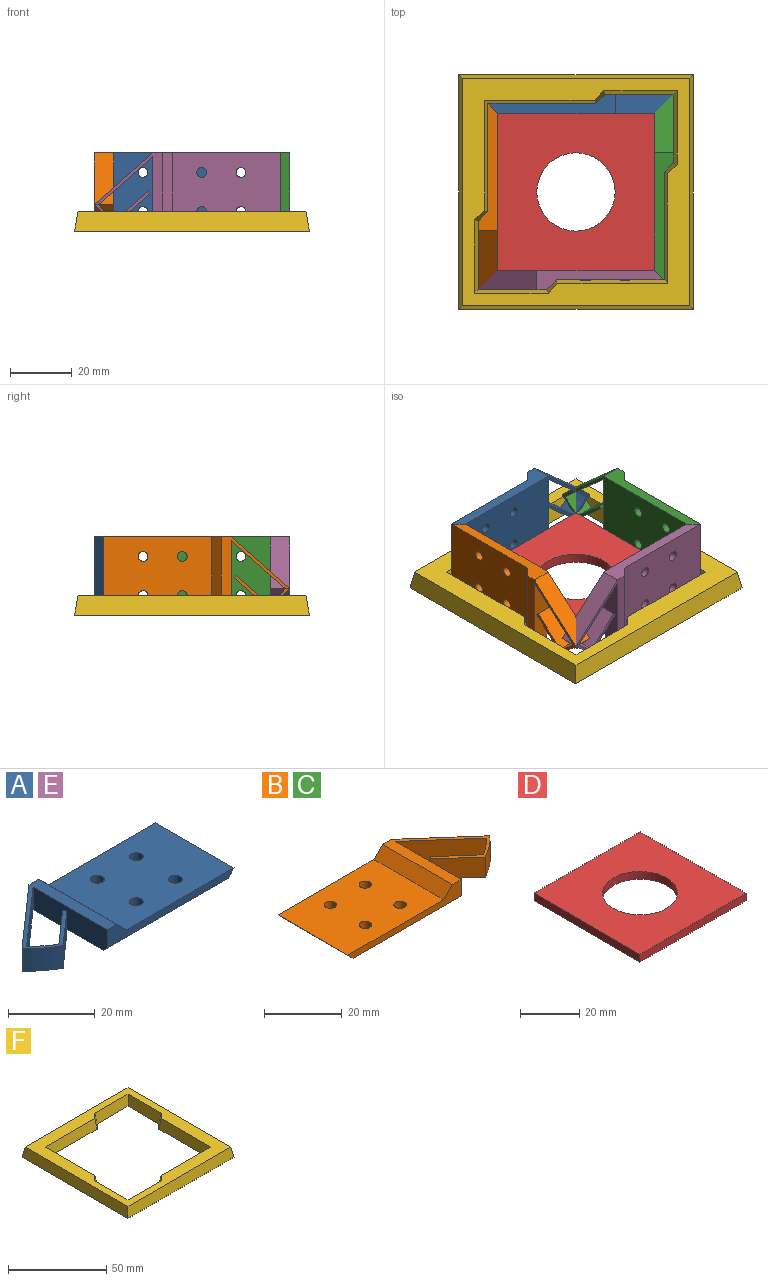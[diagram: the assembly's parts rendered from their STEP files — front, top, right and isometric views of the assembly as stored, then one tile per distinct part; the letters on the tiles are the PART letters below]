
ASSEMBLY  parts=6 mates=5
PART A: 20 faces, bbox 60.3x25.4x6.4 mm
  f0: plane 24.07x6.35mm, normal (-1,0,0), area 152mm2, adj f8,f9,f11,f12,f15
  f1: plane 41.28x6.35mm, normal (0,1,0), area 141.1mm2, adj f2,f10,f11,f12,f13,f14
  f2: plane 19.05x16.8mm, normal (-0.66,0.75,0), area 161.3mm2, adj f1,f3,f11,f12
  f3: cylinder r=25.4mm len=7.53mm, axis (0,0,-1), area 60.8mm2, adj f2,f4,f11,f12
  f4: plane 10.52x9.28mm, normal (0.66,-0.75,0), area 89.1mm2, adj f3,f5,f11,f12
  f5: plane 6.35x0.75mm, normal (0.75,0.66,0), area 6.4mm2, adj f4,f6,f11,f12
  f6: plane 10.21x9mm, normal (-0.66,0.75,0), area 86.4mm2, adj f5,f7,f11,f12
  f7: cylinder r=23.5mm len=6.35mm, axis (0,0,-1), area 47.5mm2, adj f6,f8,f11,f12
  f8: plane 17.62x15.54mm, normal (0.66,-0.75,0), area 149.2mm2, adj f0,f7,f11,f12
  f9: plane 41.28x5.08mm, normal (0,-1,0), area 91.9mm2, adj f0,f10,f12,f13,f14,f15
  f10: plane 34.93x25.4mm, normal (0,0,1), area 855.4mm2, adj f1,f9,f13,f14,f16,f17,f18,f19
  f11: plane 57.15x24.13mm, normal (0,0,-1), area 933.3mm2, adj f0,f1,f2,f3,f4,f5,f6,f7
  f12: plane 25.4x22.23mm, normal (0,0,1), area 126.3mm2, adj f0,f1,f2,f3,f4,f5,f6,f7
  f13: plane 25.4x3.18mm, normal (0.71,0,0.71), area 114mm2, adj f1,f9,f10,f12
  f14: plane 25.4x3.18mm, normal (0.71,0,-0.71), area 112.9mm2, adj f1,f9,f10,f11,f15
  f15: plane 39.37x1.27mm, normal (0,-0.71,-0.71), area 69.6mm2, adj f0,f9,f11,f14
  f16: cylinder r=1.59mm len=3.18mm, axis (0,0,1), area 31.7mm2, adj f10,f11
  f17: cylinder r=1.59mm len=3.18mm, axis (0,0,1), area 31.7mm2, adj f10,f11
  f18: cylinder r=1.59mm len=3.18mm, axis (0,0,1), area 31.7mm2, adj f10,f11
  f19: cylinder r=1.59mm len=3.18mm, axis (0,0,1), area 31.7mm2, adj f10,f11
PART B: 20 faces, bbox 60.3x25.4x6.4 mm
  f0: plane 24.07x6.35mm, normal (1,0,0), area 152mm2, adj f8,f9,f11,f12,f15
  f1: plane 41.28x6.35mm, normal (0,1,0), area 141.1mm2, adj f2,f10,f11,f12,f13,f14
  f2: plane 19.05x16.8mm, normal (0.66,0.75,0), area 161.3mm2, adj f1,f3,f11,f12
  f3: cylinder r=25.4mm len=7.53mm, axis (0,0,-1), area 60.8mm2, adj f2,f4,f11,f12
  f4: plane 10.52x9.28mm, normal (-0.66,-0.75,0), area 89.1mm2, adj f3,f5,f11,f12
  f5: plane 6.35x0.75mm, normal (-0.75,0.66,0), area 6.4mm2, adj f4,f6,f11,f12
  f6: plane 10.21x9mm, normal (0.66,0.75,0), area 86.4mm2, adj f5,f7,f11,f12
  f7: cylinder r=23.5mm len=6.35mm, axis (0,0,-1), area 47.5mm2, adj f6,f8,f11,f12
  f8: plane 17.62x15.54mm, normal (-0.66,-0.75,0), area 149.2mm2, adj f0,f7,f11,f12
  f9: plane 41.28x5.08mm, normal (0,-1,0), area 91.9mm2, adj f0,f10,f12,f13,f14,f15
  f10: plane 34.93x25.4mm, normal (0,0,1), area 855.4mm2, adj f1,f9,f13,f14,f16,f17,f18,f19
  f11: plane 57.15x24.13mm, normal (0,0,-1), area 933.3mm2, adj f0,f1,f2,f3,f4,f5,f6,f7
  f12: plane 25.4x22.23mm, normal (0,0,1), area 126.3mm2, adj f0,f1,f2,f3,f4,f5,f6,f7
  f13: plane 25.4x3.18mm, normal (-0.71,0,0.71), area 114mm2, adj f1,f9,f10,f12
  f14: plane 25.4x3.18mm, normal (-0.71,0,-0.71), area 112.9mm2, adj f1,f9,f10,f11,f15
  f15: plane 39.37x1.27mm, normal (0,-0.71,-0.71), area 69.6mm2, adj f0,f9,f11,f14
  f16: cylinder r=1.59mm len=3.18mm, axis (0,0,1), area 31.7mm2, adj f10,f11
  f17: cylinder r=1.59mm len=3.18mm, axis (0,0,1), area 31.7mm2, adj f10,f11
  f18: cylinder r=1.59mm len=3.18mm, axis (0,0,1), area 31.7mm2, adj f10,f11
  f19: cylinder r=1.59mm len=3.18mm, axis (0,0,1), area 31.7mm2, adj f10,f11
PART C: same geometry as B
PART D: 7 faces, bbox 50.8x50.8x3.2 mm
  f0: plane 50.8x3.18mm, normal (1,0,0), area 161.3mm2, adj f1,f3,f4,f5
  f1: plane 50.8x3.18mm, normal (0,1,0), area 161.3mm2, adj f0,f2,f4,f5
  f2: plane 50.8x3.18mm, normal (-1,0,0), area 161.3mm2, adj f1,f3,f4,f5
  f3: plane 50.8x3.18mm, normal (0,-1,0), area 161.3mm2, adj f0,f2,f4,f5
  f4: plane 50.8x50.8mm, normal (0,0,1), area 2073.9mm2, adj f0,f1,f2,f3,f6
  f5: plane 50.8x50.8mm, normal (0,0,-1), area 2073.9mm2, adj f0,f1,f2,f3,f6
  f6: cylinder r=12.7mm len=25.4mm, axis (0,0,1), area 253.4mm2, adj f4,f5
PART E: same geometry as A
PART F: 18 faces, bbox 76.2x76.2x6.4 mm
  f0: plane 76.2x6.35mm, normal (0.98,0,0.17), area 484.1mm2, adj f1,f15,f16,f17
  f1: plane 76.2x6.35mm, normal (0,0.98,0.17), area 484.1mm2, adj f0,f2,f16,f17
  f2: plane 76.2x6.35mm, normal (-0.98,0,0.17), area 484.1mm2, adj f1,f15,f16,f17
  f3: plane 23.81x6.35mm, normal (-0.98,0,0.17), area 148.4mm2, adj f4,f14,f16,f17
  f4: plane 6.35x4.29mm, normal (-0.7,0.7,0.17), area 29mm2, adj f3,f5,f16,f17
  f5: plane 36.04x6.35mm, normal (-0.98,0,0.17), area 227.3mm2, adj f4,f6,f16,f17
  f6: plane 36.04x6.35mm, normal (0,0.98,0.17), area 227.3mm2, adj f5,f7,f16,f17
  f7: plane 6.35x4.29mm, normal (-0.7,0.7,0.17), area 29mm2, adj f6,f8,f16,f17
  f8: plane 23.81x6.35mm, normal (0,0.98,0.17), area 148.4mm2, adj f7,f9,f16,f17
  f9: plane 23.81x6.35mm, normal (0.98,0,0.17), area 148.4mm2, adj f8,f10,f16,f17
  f10: plane 6.35x4.29mm, normal (0.7,-0.7,0.17), area 29mm2, adj f9,f11,f16,f17
  f11: plane 36.04x6.35mm, normal (0.98,0,0.17), area 227.3mm2, adj f10,f12,f16,f17
  f12: plane 36.04x6.35mm, normal (0,-0.98,0.17), area 227.3mm2, adj f11,f13,f16,f17
  f13: plane 6.35x4.29mm, normal (0.7,-0.7,0.17), area 29mm2, adj f12,f14,f16,f17
  f14: plane 23.81x6.35mm, normal (0,-0.98,0.17), area 148.4mm2, adj f3,f13,f16,f17
  f15: plane 76.2x6.35mm, normal (0,-0.98,0.17), area 484.1mm2, adj f0,f2,f16,f17
  f16: plane 73.96x73.96mm, normal (0,0,1), area 1640.7mm2, adj f0,f1,f2,f3,f4,f5,f6,f7
  f17: plane 76.2x76.2mm, normal (0,0,-1), area 2258.1mm2, adj f0,f1,f2,f3,f4,f5,f6,f7
PLACE A rot(axis=(0,-0.71,-0.71),180deg) t=(35.68,16.49,-17.66)mm
PLACE B rot(axis=(0.58,-0.58,-0.58),120deg) t=(7.1,51.41,-17.66)mm
PLACE C rot(axis=(0.58,0.58,0.58),120deg) t=(57.9,-69.24,-17.66)mm
PLACE D t=(32.5,-8.91,-29.09)mm
PLACE E rot(axis=(1,0,0),90deg) t=(29.33,-34.31,-17.66)mm
PLACE F rot(axis=(1,0,0),0deg) t=(32.5,-8.91,-30.36)mm
MATE fastened E.f11 <-> D.f3  axis (0,1,0) through (57.9,-34.31,-29.09)mm
MATE fastened F.f17 <-> B.f9  axis (0,0,-1) through (3.93,19.66,-30.36)mm
MATE fastened B.f11 <-> D.f2  axis (1,0,0) through (7.1,16.49,-29.09)mm
MATE fastened C.f11 <-> D.f0  axis (-1,0,0) through (57.9,-34.31,-29.09)mm
MATE fastened A.f11 <-> D.f1  axis (0,-1,0) through (7.1,16.49,-29.09)mm
